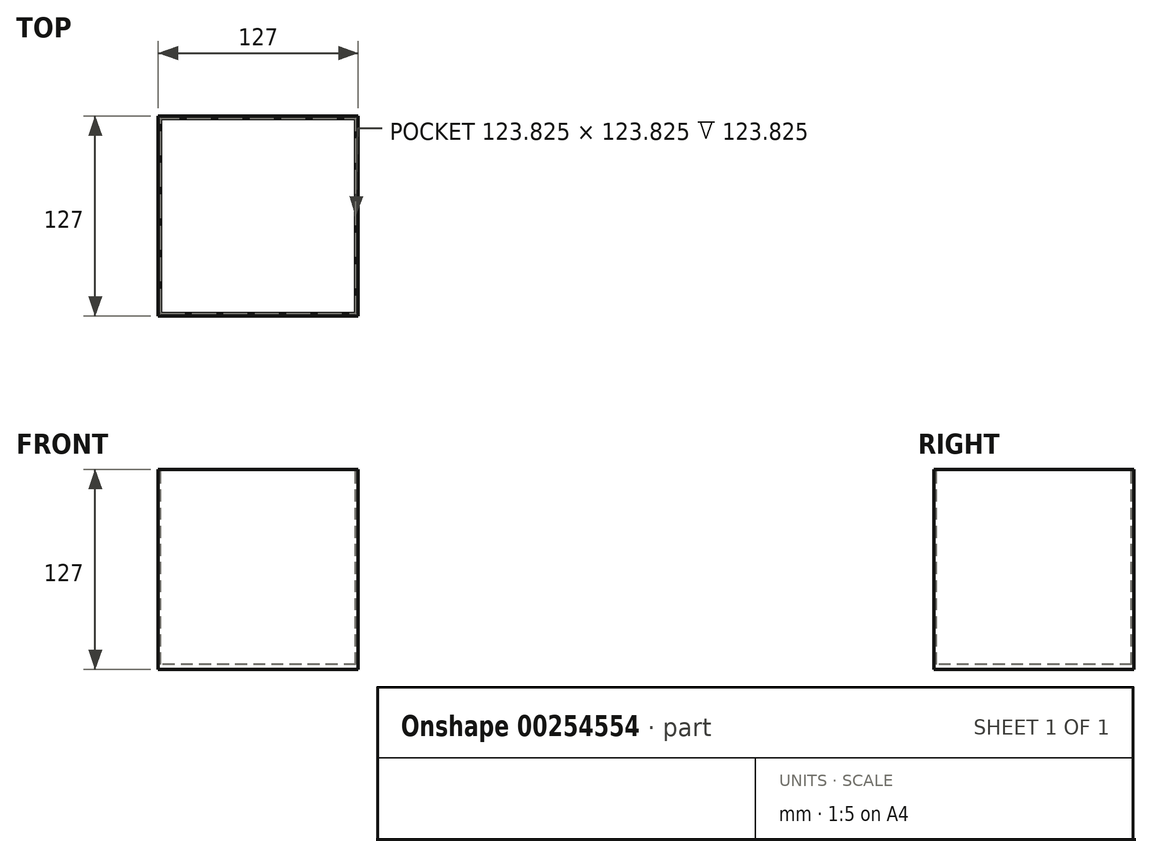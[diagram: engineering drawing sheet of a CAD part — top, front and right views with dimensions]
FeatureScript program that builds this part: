
annotation { "Feature Type Name" : "Feature", "Feature Type Description" : "" }
export const myFeature = defineFeature(function(context is Context, id is Id, definition is map)
    precondition{}
    {
        {
            var Q0;
            Q0=qCreatedBy(makeId("Front.planeOp"),FACE);
            var sketch = newSketch(context, id + "F0", { "sketchPlane" : qUnion([Q0])});
            skLineSegment(sketch, "E0.bottom", {"start": v(-63.5, -63.5) * mm, "end": v(63.5, -63.5) * mm});
            skLineSegment(sketch, "E0.top", {"start": v(-63.5, 63.5) * mm, "end": v(63.5, 63.5) * mm});
            skLineSegment(sketch, "E0.left", {"start": v(-63.5, -63.5) * mm, "end": v(-63.5, 63.5) * mm});
            skLineSegment(sketch, "E0.right", {"start": v(63.5, -63.5) * mm, "end": v(63.5, 63.5) * mm});
            skPoint(sketch, "E0.middle", {"position": v(0, 0) * mm});
            skSolve(sketch);
        }
        {
            var Q0;
            Q0 = qSketchRegion(id + "F0", true);
            extrude(context, id + "F1", {"entities" : qUnion([Q0]), "endBound" : BoundingType.SYMMETRIC, "depth" : 127 * mm});
        }
        {
            var Q0;
            Q0=makeQuery(id+"F1.opExtrude","SWEPT_FACE",FACE,{"disambiguationData":[OSD([sQuery(id+"F0.wireOp",EDGE,"E0.top")])]});
            var sketch = newSketch(context, id + "F2", { "sketchPlane" : qUnion([Q0])});
            skLineSegment(sketch, "E1.bottom", {"start": v(61.91, 61.91) * mm, "end": v(-61.91, 61.91) * mm});
            skLineSegment(sketch, "E1.top", {"start": v(61.91, -61.91) * mm, "end": v(-61.91, -61.91) * mm});
            skLineSegment(sketch, "E1.left", {"start": v(61.91, 61.91) * mm, "end": v(61.91, -61.91) * mm});
            skLineSegment(sketch, "E1.right", {"start": v(-61.91, 61.91) * mm, "end": v(-61.91, -61.91) * mm});
            skPoint(sketch, "E1.middle", {"position": v(0, 0) * mm});
            skSolve(sketch);
        }
        {
            var Q0;
            Q0 = qSketchRegion(id + "F2", true);
            extrude(context, id + "F3", {"entities" : qUnion([Q0]), "operationType" : NewBodyOperationType.REMOVE, "oppositeDirection" : true, "depth" : 123.82 * mm});
        }
    });
